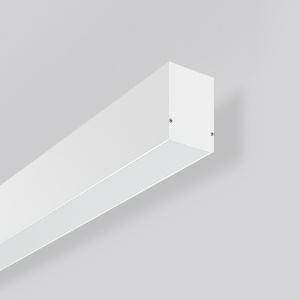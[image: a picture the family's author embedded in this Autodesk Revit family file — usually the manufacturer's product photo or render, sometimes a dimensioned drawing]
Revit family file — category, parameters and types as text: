
# Revit family: less_is_more_50_312605_002_44a9
name_source: partatom
category: Lighting Fixtures
units: mm (PartAtom-declared; Revit-internal decimal feet)

## family parameters
Cut with Voids When Loaded = No
Host = Face
Light Source = No
Part Type = Normal
Room Calculation Point = No
Round Connector Dimension = Use Diameter
Shared = No

## types (1)
- LESS IS MORE 50 (1 x LED Modul 830, 1100 lm, 3000)
    Apparent Load = 9 VA
    CIE Flux Codes = 48 80 96 100 100
    Color Rendering = 80
    Color Temperature = 3000
    Default Elevation = 1800 mm
    Description = Series: LESS IS MORE 50
Linear wall luminaires. Housing: extruded aluminium profile, powder-coated. End cap aluminium powder-coated. Diffuser made of non-yellowing plastic (PMMA), opal. Direct light emission. Suitable for Wall (surface). LED unit with integrated converter interchangeable and removable. Suitable for through-wiring. With sensors or as a safety luminaire on request. 
Colour: traffic white, matt (RAL 9016)
Length: 847 mm
Width: 67 mm
Height: 75 mm
Lamp: LED
Socket: without socket
Colour temperature: 3000K
Colour rendering index (CRI): 80
System power: 9 W
Rated luminous flux: 1100 lm
Luminous efficiency: 122 lm/W
Control gear: Regulated power supply
Protection class: I
Type of protection: IP 20
    Height = 75 mm
    Lamp = 1 x LED Modul 830
    Lamp Light Flux = 1100 lm
    Lamp count = 1
    Length = 847 mm
    Lifetime = 50000 h
    Luminous efficacy = 122 lm/W
    Manufacturer = RZB
    ModVariant = No
    Model = 312605.002
    Mounting Place = Wall
    Mounting Type = Surface mounted
    Number of Poles = 1
    OnlyDefault = Yes
    Power Factor = 1
    Product Name = LESS IS MORE 50
    Product group = Surface mounted LED linear luminaires
    ProductGroupID = 2007
    Protection Class = Protection class I
    Protection Degree = IP 20
    RLX_Detail_Level = 1
    RLX_Emergency_Light_Flux = 0 lm
    RLX_Emergency_Type = 0
    RLX_Emergency_Type_DB = No
    RlxData = <blob elided: 35093 chars, md5=1cac3573>
    Socket = socket
    Standby Power = 0 W
    System Light Flux = 1100 lm
    System Power = 9 W
    Type Comments = Product without accessories
    Type Image = 312606.002.jpg
    URL = http://relux.com
    VarID = ---
    Voltage = 0 V
    Weight = 0.00 kg
    Width = 67 mm

## geometry (parser evidence)
native form markers: Blend x4, Sweep x8
no freeform markers — native parametric forms only
